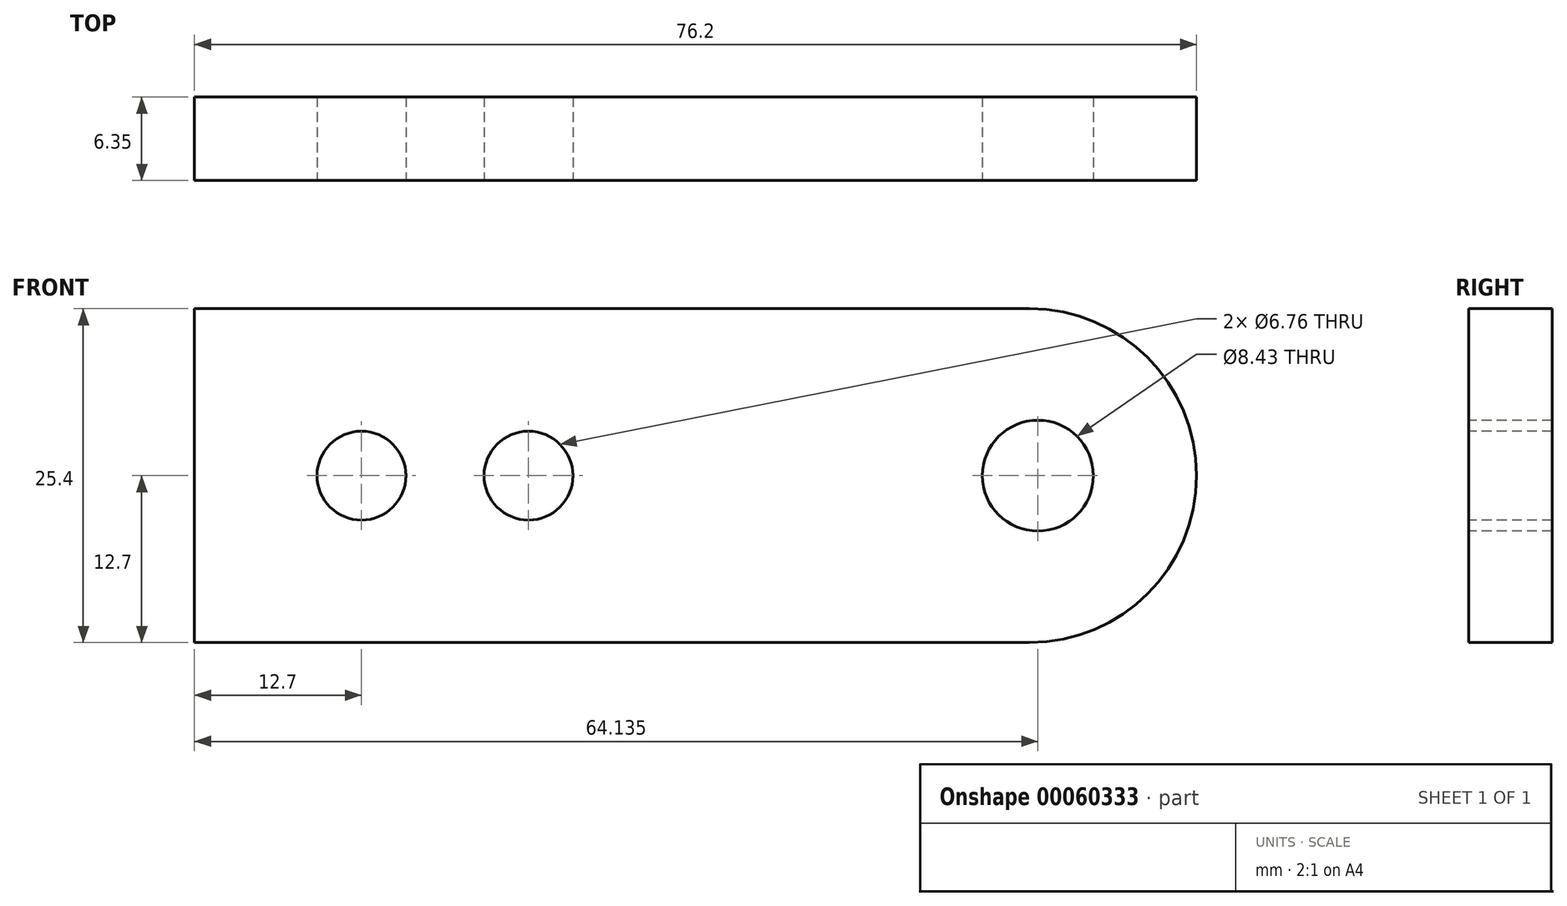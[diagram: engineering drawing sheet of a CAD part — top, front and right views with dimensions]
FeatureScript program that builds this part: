
annotation { "Feature Type Name" : "Feature", "Feature Type Description" : "" }
export const myFeature = defineFeature(function(context is Context, id is Id, definition is map)
    precondition{}
    {
        {
            var Q0;
            Q0=qCreatedBy(makeId("Front.planeOp"),FACE);
            var sketch = newSketch(context, id + "F0", { "sketchPlane" : qUnion([Q0])});
            skLineSegment(sketch, "E0.rect.bottom", {"start": v(25.4, -12.7) * mm, "end": v(-38.1, -12.7) * mm});
            skLineSegment(sketch, "E0.rect.top", {"start": v(25.4, 12.7) * mm, "end": v(-38.1, 12.7) * mm});
            skLineSegment(sketch, "E0.rect.left", {"start": v(38.1, 0) * mm, "end": v(38.1, 0) * mm});
            skLineSegment(sketch, "E0.rect.right", {"start": v(-38.1, -12.7) * mm, "end": v(-38.1, 12.7) * mm});
            skPoint(sketch, "E0.rect.middle", {"position": v(0, 0) * mm});
            skPoint(sketch, "E1.visualSharp", {"position": v(38.1, 12.7) * mm});
            skArc(sketch, "E1.filletArc", {"start": v(38.1, 0) * mm, "mid": v(34.38, 8.98) * mm, "end": v(25.4, 12.7) * mm});
            skPoint(sketch, "E2.visualSharp", {"position": v(38.1, -12.7) * mm});
            skArc(sketch, "E2.filletArc", {"start": v(25.4, -12.7) * mm, "mid": v(34.38, -8.98) * mm, "end": v(38.1, 0) * mm});
            skSolve(sketch);
        }
        {
            var Q0;
            Q0 = qSketchRegion(id + "F0", true);
            extrude(context, id + "F1", {"entities" : qUnion([Q0]), "depth" : 6.35 * mm});
        }
        {
            var Q0;
            Q0=makeQuery(id+"F1.opExtrude","CAP_FACE",FACE,{"disambiguationData":[OSD([sQuery(id+"F0.wireOp",EDGE,"E0.rect.bottom"),sQuery(id+"F0.wireOp",EDGE,"E0.rect.top"),sQuery(id+"F0.wireOp",EDGE,"E0.rect.right"),sQuery(id+"F0.wireOp",EDGE,"E1.filletArc"),sQuery(id+"F0.wireOp",EDGE,"E2.filletArc")])],"isStart":false});
            var sketch = newSketch(context, id + "F2", { "sketchPlane" : qUnion([Q0])});
            skPoint(sketch, "E3", {"position": v(26.04, 0) * mm});
            skPoint(sketch, "E4", {"position": v(-25.4, 0) * mm});
            skPoint(sketch, "E5", {"position": v(-12.7, 0) * mm});
            skSolve(sketch);
        }
        {
            var Q0;
            Q0=sQuery(id+"F2.wireOp",VERTEX,"E3");
            var Q1;
            Q1=makeQuery(id+"F1.opExtrude","SWEPT_BODY",BODY,{"disambiguationData":[OSD([sQuery(id+"F0.wireOp",EDGE,"E0.rect.bottom"),sQuery(id+"F0.wireOp",EDGE,"E0.rect.top"),sQuery(id+"F0.wireOp",EDGE,"E0.rect.right"),sQuery(id+"F0.wireOp",EDGE,"E1.filletArc"),sQuery(id+"F0.wireOp",EDGE,"E2.filletArc")])]});
            hole(context, id + "F3", {"style" : HoleStyle.SIMPLE, "holeDiameter" : 8.43 * mm, "endStyle" : HoleEndStyle.THROUGH, "locations" : qUnion([Q0]), "scope" : qUnion([Q1])});
        }
        {
            var Q0;
            Q0=sQuery(id+"F2.wireOp",VERTEX,"E4");
            var Q1;
            Q1=sQuery(id+"F2.wireOp",VERTEX,"E5");
            var Q2;
            Q2=makeQuery(id+"F1.opExtrude","SWEPT_BODY",BODY,{"disambiguationData":[OSD([sQuery(id+"F0.wireOp",EDGE,"E0.rect.bottom"),sQuery(id+"F0.wireOp",EDGE,"E0.rect.top"),sQuery(id+"F0.wireOp",EDGE,"E0.rect.right"),sQuery(id+"F0.wireOp",EDGE,"E1.filletArc"),sQuery(id+"F0.wireOp",EDGE,"E2.filletArc")])]});
            hole(context, id + "F4", {"style" : HoleStyle.SIMPLE, "holeDiameter" : 6.76 * mm, "endStyle" : HoleEndStyle.THROUGH, "locations" : qUnion([Q0, Q1]), "scope" : qUnion([Q2])});
        }
    });
